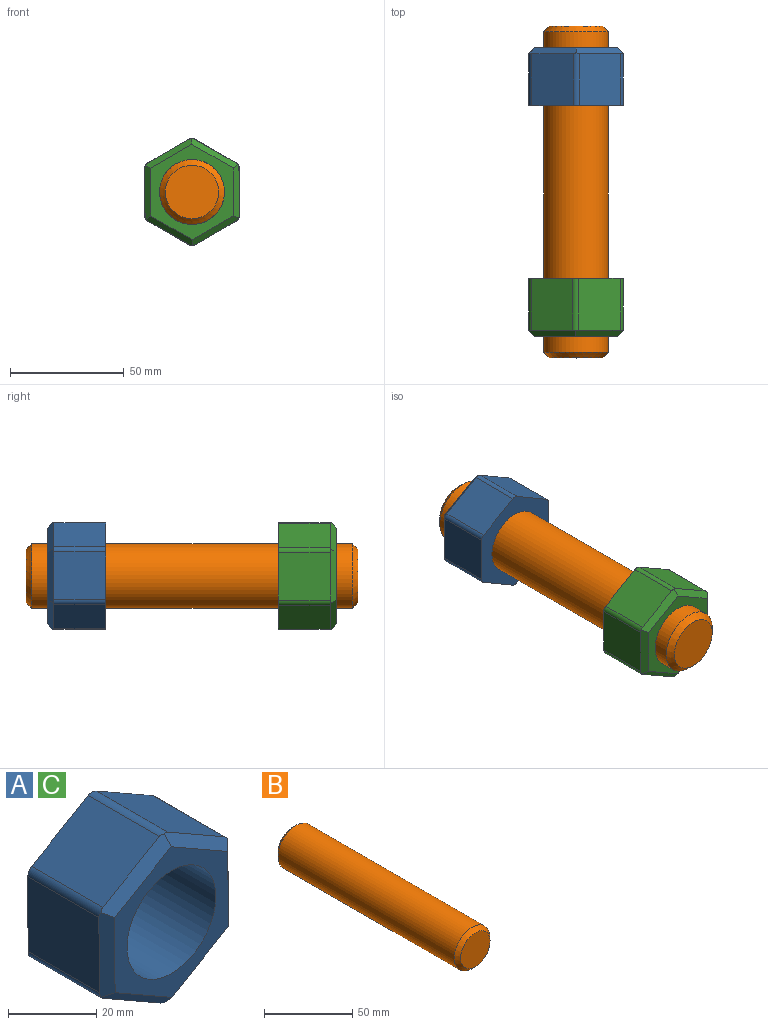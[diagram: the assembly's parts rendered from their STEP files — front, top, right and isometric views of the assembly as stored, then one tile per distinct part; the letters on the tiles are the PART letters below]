
ASSEMBLY  parts=3 mates=2
PART A: 21 faces, bbox 41.5x25.4x47.1 mm
  f0: plane 22.86x18.13mm, normal (-0.5,0,0.86), area 479.9mm2, adj f8,f12,f15,f20
  f1: plane 22.86x20.99mm, normal (-1,0,0), area 479.9mm2, adj f8,f10,f15,f16
  f2: plane 22.86x18.23mm, normal (-0.5,0,-0.87), area 479.9mm2, adj f8,f9,f16,f17
  f3: plane 22.86x18.13mm, normal (0.5,0,-0.86), area 479.9mm2, adj f8,f11,f17,f18
  f4: plane 22.86x20.99mm, normal (1,0,0), area 479.9mm2, adj f8,f13,f18,f19
  f5: cylinder r=14.29mm len=28.58mm, axis (0,1,0), area 2280.2mm2, adj f7,f8
  f6: plane 22.86x18.23mm, normal (0.5,0,0.87), area 479.9mm2, adj f8,f14,f19,f20
  f7: plane 41.99x36.46mm, normal (0,-1,0), area 503.8mm2, adj f5,f9,f10,f11,f12,f13,f14
  f8: plane 47.07x41.54mm, normal (0,1,0), area 844mm2, adj f0,f1,f2,f3,f4,f5,f6,f15
  f9: plane 20.43x12.96mm, normal (-0.35,-0.71,-0.61), area 80.2mm2, adj f2,f7,f10,f11,f16,f17
  f10: plane 23.53x2.63mm, normal (-0.71,-0.71,0), area 80.2mm2, adj f1,f7,f9,f12,f15,f16
  f11: plane 20.34x13.12mm, normal (0.36,-0.71,-0.61), area 80.2mm2, adj f3,f7,f9,f13,f17,f18
  f12: plane 20.34x13.12mm, normal (-0.36,-0.71,0.61), area 80.2mm2, adj f0,f7,f10,f14,f15,f20
  f13: plane 23.53x2.63mm, normal (0.71,-0.71,0), area 80.2mm2, adj f4,f7,f11,f14,f18,f19
  f14: plane 20.43x12.96mm, normal (0.35,-0.71,0.61), area 80.2mm2, adj f6,f7,f12,f13,f19,f20
  f15: cylinder r=2.54mm len=23.2mm, axis (0,1,0), area 61.1mm2, adj f0,f1,f8,f10,f12
  f16: cylinder r=2.54mm len=23.2mm, axis (0,1,0), area 61.1mm2, adj f1,f2,f8,f9,f10
  f17: cylinder r=2.54mm len=23.2mm, axis (0,1,0), area 61.1mm2, adj f2,f3,f8,f9,f11
  f18: cylinder r=2.54mm len=23.2mm, axis (0,1,0), area 61.1mm2, adj f3,f4,f8,f11,f13
  f19: cylinder r=2.54mm len=23.2mm, axis (0,1,0), area 61.1mm2, adj f4,f6,f8,f13,f14
  f20: cylinder r=2.54mm len=23.2mm, axis (0,1,0), area 61.1mm2, adj f0,f6,f8,f12,f14
PART B: 5 faces, bbox 28.6x146.1x28.6 mm
  f0: cylinder r=14.29mm len=140.97mm, axis (0,1,0), area 12655mm2, adj f3,f4
  f1: plane 23.5x23.5mm, normal (0,-1,0), area 433.6mm2, adj f3
  f2: plane 23.5x23.5mm, normal (0,1,0), area 433.6mm2, adj f4
  f3: cone r=11.75mm half-angle=45deg, axis (0,1,0), area 293.8mm2, adj f0,f1
  f4: cone r=14.29mm half-angle=45deg, axis (0,-1,0), area 293.8mm2, adj f0,f2
PART C: same geometry as A
PLACE A rot(axis=(1,0,0),180deg) t=(11.12,101.17,8.97)mm
PLACE B t=(11.12,136.16,8.97)mm
PLACE C t=(11.12,25.1,8.97)mm
MATE planar A.f5 <-> C.f5  axis (0,-1,0) through (11.12,101.17,8.97)mm
MATE fastened B.f0 <-> C.f5  axis (0,-1,0) through (11.12,-9.89,8.97)mm
